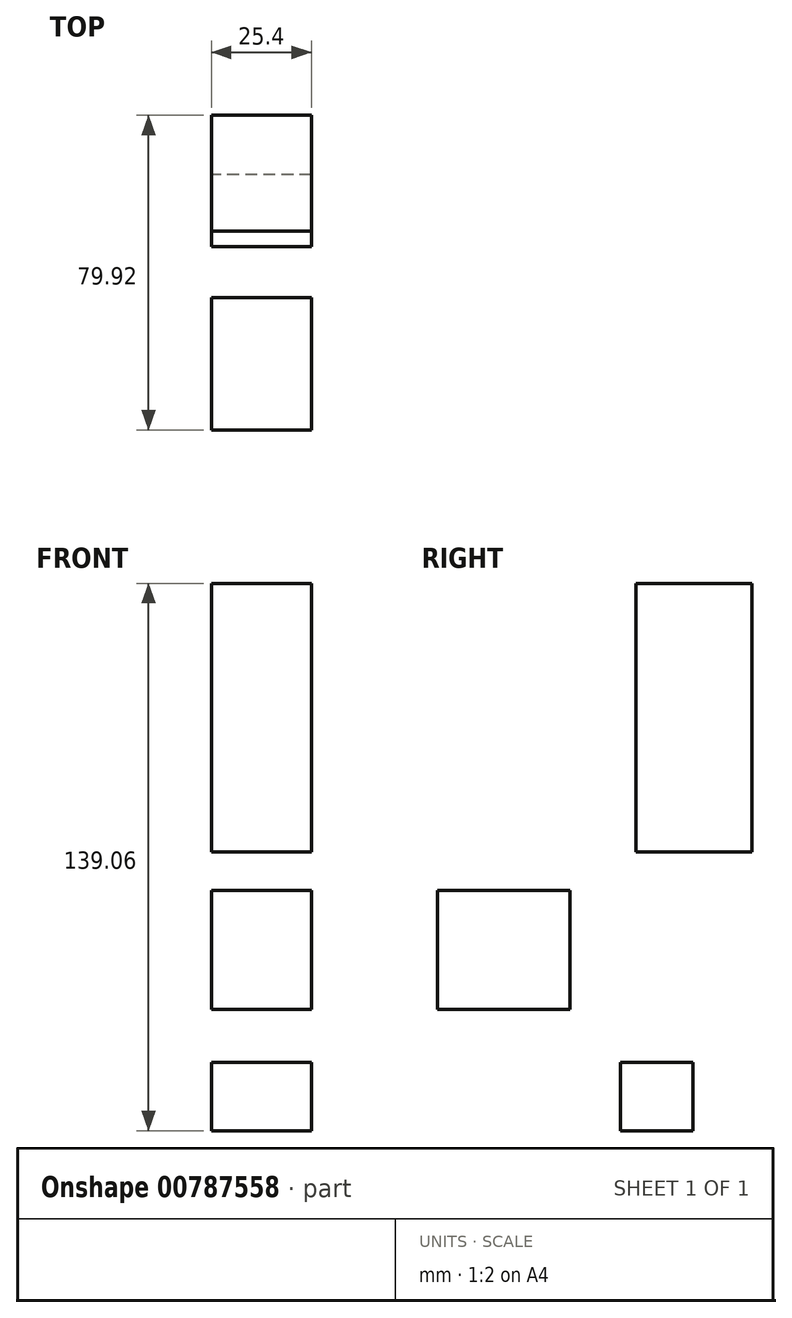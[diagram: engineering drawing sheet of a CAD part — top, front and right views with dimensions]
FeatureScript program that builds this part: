
annotation { "Feature Type Name" : "Feature", "Feature Type Description" : "" }
export const myFeature = defineFeature(function(context is Context, id is Id, definition is map)
    precondition{}
    {
        {
            var Q0;
            Q0=qCreatedBy(makeId("Right.planeOp"),FACE);
            var sketch = newSketch(context, id + "F0", { "sketchPlane" : qUnion([Q0])});
            skLineSegment(sketch, "E0.bottom", {"start": v(-14.38, 19.03) * mm, "end": v(19.28, 19.03) * mm});
            skLineSegment(sketch, "E0.top", {"start": v(-14.38, -11.23) * mm, "end": v(19.28, -11.23) * mm});
            skLineSegment(sketch, "E0.left", {"start": v(-14.38, 19.03) * mm, "end": v(-14.38, -11.23) * mm});
            skLineSegment(sketch, "E0.right", {"start": v(19.28, 19.03) * mm, "end": v(19.28, -11.23) * mm});
            skLineSegment(sketch, "E1.bottom", {"start": v(50.5, -42.03) * mm, "end": v(32.13, -42.03) * mm});
            skLineSegment(sketch, "E1.top", {"start": v(50.5, -24.72) * mm, "end": v(32.13, -24.72) * mm});
            skLineSegment(sketch, "E1.left", {"start": v(50.5, -42.03) * mm, "end": v(50.5, -24.72) * mm});
            skLineSegment(sketch, "E1.right", {"start": v(32.13, -42.03) * mm, "end": v(32.13, -24.72) * mm});
            skLineSegment(sketch, "E2.bottom", {"start": v(36.1, 28.76) * mm, "end": v(65.54, 28.76) * mm});
            skLineSegment(sketch, "E2.top", {"start": v(36.1, 97.03) * mm, "end": v(65.54, 97.03) * mm});
            skLineSegment(sketch, "E2.left", {"start": v(36.1, 28.76) * mm, "end": v(36.1, 97.03) * mm});
            skLineSegment(sketch, "E2.right", {"start": v(65.54, 28.76) * mm, "end": v(65.54, 97.03) * mm});
            skSolve(sketch);
        }
        {
            var Q0;
            Q0=makeQuery(id+"F0.imprint","IMPRINT",FACE,{"disambiguationData":[TD([[makeQuery(id+"F0.imprint","IMPRINT",EDGE,{"derivedFrom":sQuery(id+"F0.wireOp",EDGE,"E0.bottom")}),-1.0]])]});
            extrude(context, id + "F1", {"entities" : qUnion([Q0]), "depth" : 25.4 * mm, "offsetDistance" : 25.4 * mm});
        }
        {
            var Q0;
            Q0=makeQuery(id+"F1.opExtrude","CAP_FACE",FACE,{"disambiguationData":[OSD([sQuery(id+"F0.wireOp",EDGE,"E0.bottom"),sQuery(id+"F0.wireOp",EDGE,"E0.top"),sQuery(id+"F0.wireOp",EDGE,"E0.left"),sQuery(id+"F0.wireOp",EDGE,"E0.right")])],"isStart":false});
            fillet(context, id + "F2", {"entities" : qUnion([Q0]), "radius" : 5.08 * mm, "tangentPropagation" : true, "allowEdgeOverflow" : false});
        }
        {
            var Q0;
            Q0=makeQuery(id+"F2.opFillet","BLEND_FACE",FACE,{"disambiguationData":[OSD([sQuery(id+"F0.wireOp",EDGE,"E0.left")])]});
            var Q1;
            Q1=makeQuery(id+"F1.opExtrude","SWEPT_FACE",FACE,{"disambiguationData":[OSD([sQuery(id+"F0.wireOp",EDGE,"E0.left")])]});
            var Q2;
            Q2=makeQuery(id+"F1.opExtrude","CAP_FACE",FACE,{"disambiguationData":[OSD([sQuery(id+"F0.wireOp",EDGE,"E0.bottom"),sQuery(id+"F0.wireOp",EDGE,"E0.top"),sQuery(id+"F0.wireOp",EDGE,"E0.left"),sQuery(id+"F0.wireOp",EDGE,"E0.right")])],"isStart":true});
            var Q3;
            Q3=makeQuery(id+"F1.opExtrude","SWEPT_FACE",FACE,{"disambiguationData":[OSD([sQuery(id+"F0.wireOp",EDGE,"E0.top")])]});
            var Q4;
            Q4=makeQuery(id+"F1.opExtrude","CAP_FACE",FACE,{"disambiguationData":[OSD([sQuery(id+"F0.wireOp",EDGE,"E0.bottom"),sQuery(id+"F0.wireOp",EDGE,"E0.top"),sQuery(id+"F0.wireOp",EDGE,"E0.left"),sQuery(id+"F0.wireOp",EDGE,"E0.right")])],"isStart":false});
            shell(context, id + "F3", {"entities" : qUnion([Q0, Q1, Q2, Q3, Q4]), "thickness" : 2.54 * mm});
        }
        {
            var Q0;
            Q0 = qSketchRegion(id + "F0", true);
            extrude(context, id + "F4", {"entities" : qUnion([Q0]), "operationType" : NewBodyOperationType.ADD, "depth" : 25.4 * mm, "offsetDistance" : 25.4 * mm});
        }
    });
